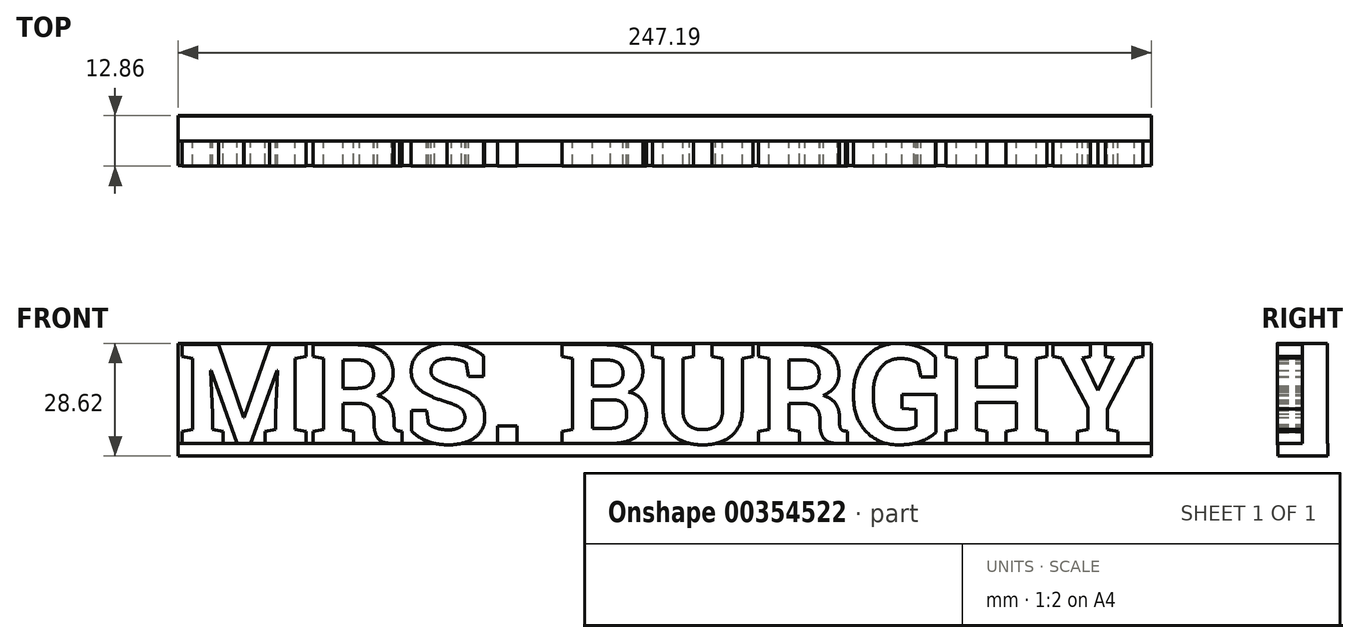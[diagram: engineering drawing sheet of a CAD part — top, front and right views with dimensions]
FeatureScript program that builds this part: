
annotation { "Feature Type Name" : "Feature", "Feature Type Description" : "" }
export const myFeature = defineFeature(function(context is Context, id is Id, definition is map)
    precondition{}
    {
        {
            var Q0;
            Q0=qCreatedBy(makeId("Front.planeOp"),FACE);
            var sketch = newSketch(context, id + "F0", { "sketchPlane" : qUnion([Q0])});
            skText(sketch, "E0", { "text": "MRS. BURGHY", "fontName": "RobotoSlab-Bold.ttf"});
            const initialGuessF0  = {"E0": [0, 0, 1, 0, 0.0254]};
            skSetInitialGuess(sketch, initialGuessF0);
            skSolve(sketch);
        }
        {
            var Q0;
            Q0=qCreatedBy(makeId("Front.planeOp"),FACE);
            var sketch = newSketch(context, id + "F1", { "sketchPlane" : qUnion([Q0])});
            skLineSegment(sketch, "E1.bottom", {"start": v(0, 0) * mm, "end": v(247.2, 0) * mm});
            skLineSegment(sketch, "E1.top", {"start": v(0, 25.4) * mm, "end": v(247.2, 25.4) * mm});
            skLineSegment(sketch, "E1.left", {"start": v(0, 0) * mm, "end": v(0, 25.4) * mm});
            skLineSegment(sketch, "E1.right", {"start": v(247.2, 0) * mm, "end": v(247.2, 25.4) * mm});
            skSolve(sketch);
        }
        {
            var Q0;
            Q0 = qSketchRegion(id + "F1", true);
            extrude(context, id + "F2", {"entities" : qUnion([Q0]), "oppositeDirection" : true, "depth" : 6.35 * mm});
        }
        {
            var Q0;
            Q0 = qSketchRegion(id + "F0", true);
            extrude(context, id + "F3", {"entities" : qUnion([Q0]), "operationType" : NewBodyOperationType.ADD, "depth" : 6.35 * mm});
        }
        {
            var Q0;
            Q0=qCreatedBy(makeId("Top.planeOp"),FACE);
            var sketch = newSketch(context, id + "F4", { "sketchPlane" : qUnion([Q0])});
            skLineSegment(sketch, "E2.bottom", {"start": v(0, 6.51) * mm, "end": v(247.2, 6.51) * mm});
            skLineSegment(sketch, "E2.top", {"start": v(0, -6.19) * mm, "end": v(247.2, -6.19) * mm});
            skLineSegment(sketch, "E2.left", {"start": v(0, 6.51) * mm, "end": v(0, -6.19) * mm});
            skLineSegment(sketch, "E2.right", {"start": v(247.2, 6.51) * mm, "end": v(247.2, -6.19) * mm});
            skSolve(sketch);
        }
        {
            var Q0;
            Q0 = qSketchRegion(id + "F4", true);
            extrude(context, id + "F5", {"entities" : qUnion([Q0]), "operationType" : NewBodyOperationType.ADD, "oppositeDirection" : true, "depth" : 3.17 * mm});
        }
    });
